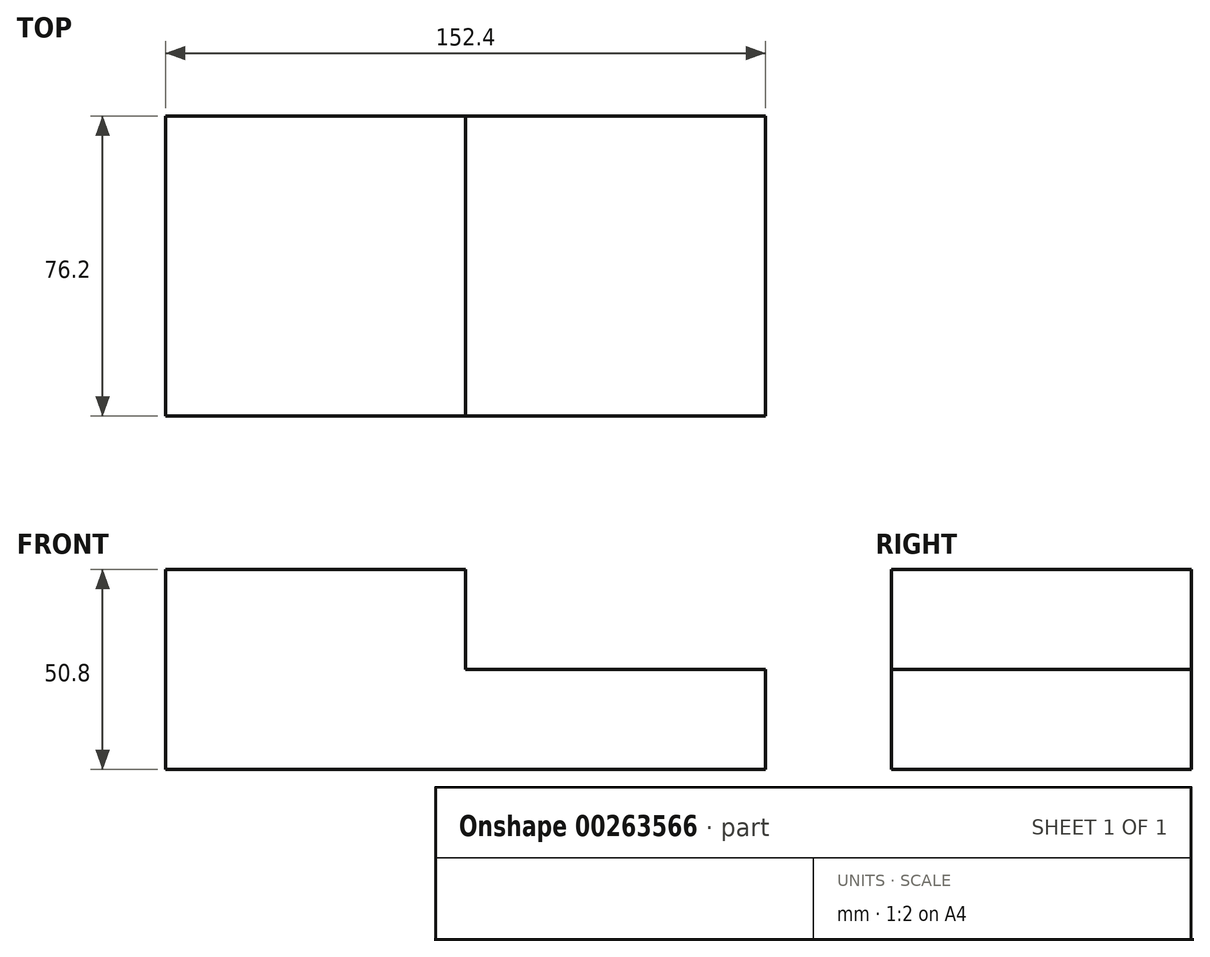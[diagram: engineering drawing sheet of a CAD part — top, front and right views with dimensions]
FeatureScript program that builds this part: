
annotation { "Feature Type Name" : "Feature", "Feature Type Description" : "" }
export const myFeature = defineFeature(function(context is Context, id is Id, definition is map)
    precondition{}
    {
        {
            var Q0;
            Q0=qCreatedBy(makeId("Front.planeOp"),FACE);
            var sketch = newSketch(context, id + "F0", { "sketchPlane" : qUnion([Q0])});
            skLineSegment(sketch, "E0", {"start": v(-65.8, 0) * mm, "end": v(-65.8, -50.8) * mm});
            skLineSegment(sketch, "E1", {"start": v(-65.8, -50.8) * mm, "end": v(86.6, -50.8) * mm});
            skLineSegment(sketch, "E2", {"start": v(-65.8, 0) * mm, "end": v(10.4, 0) * mm});
            skLineSegment(sketch, "E3", {"start": v(10.4, 0) * mm, "end": v(10.4, -25.4) * mm});
            skLineSegment(sketch, "E4", {"start": v(10.4, -25.4) * mm, "end": v(86.6, -25.4) * mm});
            skLineSegment(sketch, "E5", {"start": v(86.6, -25.4) * mm, "end": v(86.6, -50.8) * mm});
            skSolve(sketch);
        }
        {
            var Q0;
            Q0 = qSketchRegion(id + "F0", true);
            extrude(context, id + "F1", {"entities" : qUnion([Q0]), "depth" : 76.2 * mm});
        }
    });
